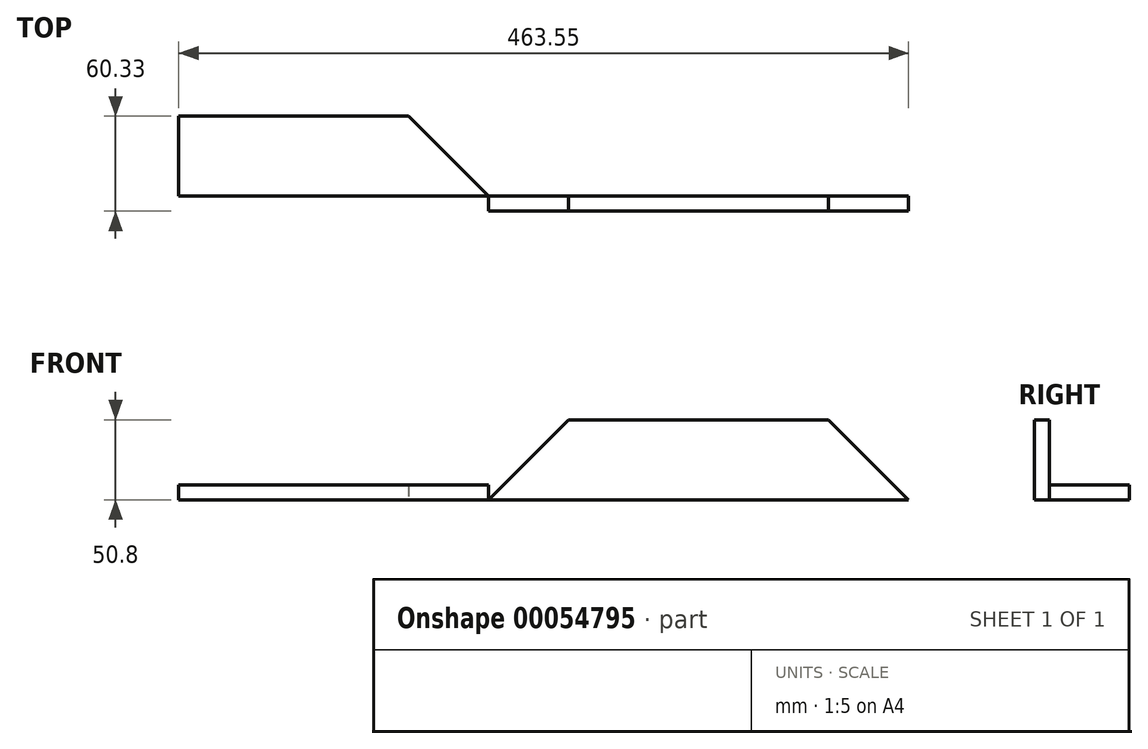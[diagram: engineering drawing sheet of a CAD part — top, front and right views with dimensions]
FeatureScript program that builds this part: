
annotation { "Feature Type Name" : "Feature", "Feature Type Description" : "" }
export const myFeature = defineFeature(function(context is Context, id is Id, definition is map)
    precondition{}
    {
        {
            var Q0;
            Q0=qCreatedBy(makeId("Front.planeOp"),FACE);
            var sketch = newSketch(context, id + "F0", { "sketchPlane" : qUnion([Q0])});
            skPoint(sketch, "E0.0", {"position": v(0, 0) * mm});
            skLineSegment(sketch, "E1.bottom", {"start": v(0, 0) * mm, "end": v(266.7, 0) * mm});
            skLineSegment(sketch, "E1.top", {"start": v(0, 50.8) * mm, "end": v(266.7, 50.8) * mm});
            skLineSegment(sketch, "E1.left", {"start": v(0, 0) * mm, "end": v(0, 50.8) * mm});
            skLineSegment(sketch, "E1.right", {"start": v(266.7, 0) * mm, "end": v(266.7, 50.8) * mm});
            skSolve(sketch);
        }
        {
            var Q0;
            Q0=makeQuery(id+"F0.imprint","IMPRINT",FACE,{"disambiguationData":[TD([[makeQuery(id+"F0.imprint","IMPRINT",EDGE,{"derivedFrom":sQuery(id+"F0.wireOp",EDGE,"E1.bottom")}),1.0]])]});
            extrude(context, id + "F1", {"entities" : qUnion([Q0]), "depth" : 9.52 * mm});
        }
        {
            var Q0;
            Q0=makeQuery(id+"F1.opExtrude","SWEPT_EDGE",EDGE,{"disambiguationData":[OSD([sQuery(id+"F0.wireOp",EDGE,"E1.top"),sQuery(id+"F0.wireOp",EDGE,"E1.right")])]});
            var Q1;
            Q1=makeQuery(id+"F1.opExtrude","SWEPT_EDGE",EDGE,{"disambiguationData":[OSD([sQuery(id+"F0.wireOp",EDGE,"E1.top"),sQuery(id+"F0.wireOp",EDGE,"E1.left")])]});
            chamfer(context, id + "F2", {"entities" : qUnion([Q0, Q1]), "width" : 50.8 * mm, "tangentPropagation" : true});
        }
        {
            var Q0;
            Q0=qCreatedBy(makeId("Top.planeOp"),FACE);
            var sketch = newSketch(context, id + "F3", { "sketchPlane" : qUnion([Q0])});
            skLineSegment(sketch, "E2.bottom", {"start": v(0, 0) * mm, "end": v(-196.85, 0) * mm});
            skLineSegment(sketch, "E2.top", {"start": v(0, 50.8) * mm, "end": v(-196.85, 50.8) * mm});
            skLineSegment(sketch, "E2.left", {"start": v(0, 0) * mm, "end": v(0, 50.8) * mm});
            skLineSegment(sketch, "E2.right", {"start": v(-196.85, 0) * mm, "end": v(-196.85, 50.8) * mm});
            skSolve(sketch);
        }
        {
            var Q0;
            Q0=makeQuery(id+"F3.imprint","IMPRINT",FACE,{"disambiguationData":[TD([[makeQuery(id+"F3.imprint","IMPRINT",EDGE,{"derivedFrom":sQuery(id+"F3.wireOp",EDGE,"E2.bottom")}),-1.0]])]});
            extrude(context, id + "F4", {"entities" : qUnion([Q0]), "depth" : 9.52 * mm});
        }
        {
            var Q0;
            Q0=makeQuery(id+"F4.opExtrude","SWEPT_EDGE",EDGE,{"disambiguationData":[OSD([sQuery(id+"F3.wireOp",EDGE,"E2.top"),sQuery(id+"F3.wireOp",EDGE,"E2.left")])]});
            chamfer(context, id + "F5", {"entities" : qUnion([Q0]), "width" : 50.8 * mm, "tangentPropagation" : true});
        }
    });
